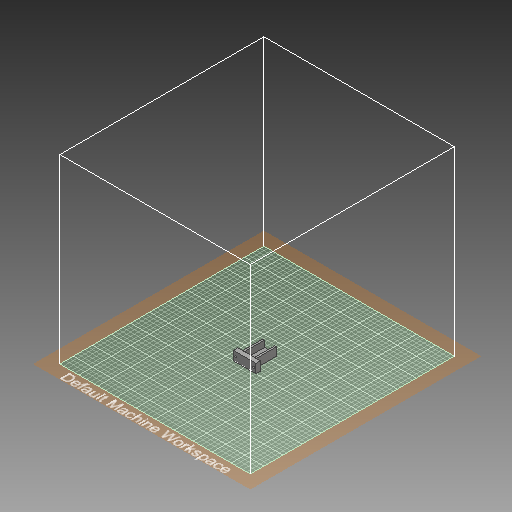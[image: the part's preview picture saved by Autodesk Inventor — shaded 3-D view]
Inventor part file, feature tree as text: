
AUTODESK INVENTOR PART (.ipt)
format: ipt  version: 2019 (Build 230136000, 136)  size: 320,512 bytes
history: native  units: mm
features: extrude x6, sketch x6, projected_geometry x1
ambient origin geometry x8: Origin, YZ Plane, XZ Plane, XY Plane, X Axis, Y Axis, Z Axis, Center Point
bodies: Body1 (feature_tree)
feature tree (13):
  extrude  "Extrusion3"  Depth=50.0mm
  extrude  "Extrusion4"  Depth=22.0mm
  extrude  "Extrusion5"  Depth=5.0mm
  extrude  "Extrusion6"  Depth=13.0mm
  extrude  "Extrusion7"  Depth=55.0mm
  extrude  "Extrusion8"  Depth=2.0mm
  sketch  "Sketch2"  dims[d10=20.0mm d11=50.0mm]
  sketch  "Sketch3"  dims[d12=10.0mm d13=0.0mm d14=22.0mm]
  projected_geometry  "Projected Loop1"
  sketch  "Sketch4"  dims[d15=5.0mm d16=5.0mm]
  sketch  "Sketch5"  dims[d17=0.5mm d18=13.0mm]
  sketch  "Sketch6"  dims[d19=55.0mm d20=0.0mm d21=4.25mm]
  sketch  "Sketch7"  dims[d23=13.0mm d24=0.0mm d26=4.25mm d27=10.0mm d28=5.0mm d29=10.0mm d30=0.0mm d32=34.875mm d33=3.25mm d34=3.25mm d35=19.0mm d36=31.0mm d37=2.8mm d38=10.0mm d39=0.0mm d40=6.0mm d41=30.0mm d42=2.0mm d43=0.0mm]
